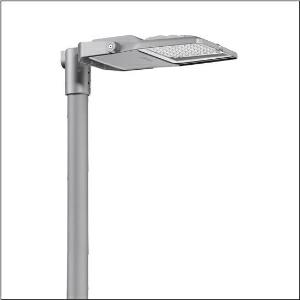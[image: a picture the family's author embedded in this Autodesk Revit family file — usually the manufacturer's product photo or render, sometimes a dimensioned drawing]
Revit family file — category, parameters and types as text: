
# Revit family: floodlight_fl_21_iq_mini___pl64_5xa7771b4e3a_3408
name_source: partatom
category: Lighting Fixtures
units: mm (PartAtom-declared; Revit-internal decimal feet)

## family parameters
Cut with Voids When Loaded = No
Host = Face
Light Source = No
Part Type = Normal
Room Calculation Point = No
Round Connector Dimension = Use Diameter
Shared = No

## types (1)
- --- (1 x LED, 6270 lm, 45.5 W, 4000K)
    Apparent Load = 46 VA
    CIE Flux Codes = 28 80 98 100 100
    Color Rendering = 70
    Color Temperature = 4000K
    Default Elevation = 1800 mm
    Description = Floodlight FL 21 iQ mini, floodlight, primary light control with lens, of PMMA, primary optical cover: protective disc, of toughened safety glass, transparent, light distribution: PL64, light emission: direct distribution, installation type: surface-mounted, LED, High Power LED, rated luminous flux: 6.270lm, luminous efficacy: 138lm/W, light colour: 740, colour temperature: 4000K, control: Auto-Match, Temp-Guard, Lumen-Switch, Night-Set, Smart-Wire, Light-Fading, Desk-Remote (wireless, voltage-free reading and setting of iQ features in the workshop via application-optimized NFC function/RFID function), optimised constant luminous flux control (CLO 2.0), with terminal, 6-pole, mains connection: 220..240V, AC, 50/60Hz, start of lifetime: 46W, end of service life: 48W, reduction: 22W, luminaire housing, of diecast aluminium, powder-coated, Siteco® metallic grey (DB 702S), corrosivity category C5 mid according to DIN EN ISO 12944, sealing non-destructively replaceable, please order mast flange separately, mast bracket, of steel, galvanised, powder-coated, Siteco® metallic grey (DB 702S), protection rating (complete): IP66, insulation class (complete): insulation class II (safety insulation), certification: CE, ENEC, VDE, protection symbol: D, impact resistance: IK08, permissible operating ambient temperature: -40..+40°C, permissible operating ambient temperature for outdoor applications: -40..+50°C, standard: DIN EN 12944, LABS conformity tested according to VDMA 24364:2018-05, packaging unit: 1 piece

Light Distribution: PL64
    Height = 70 mm
    Lamp = 1 x LED
    Lamp Light Flux = 6270 lm
    Lamp Power = 45.5 W
    Lamp count = 1
    Length = 485 mm
    Luminous efficacy = 138 lm/W
    Manufacturer = Siteco
    ModVariant = No
    Model = 5XA7771B4E3A
    Number of Poles = 1
    OnlyDefault = Yes
    Power Factor = 1
    Product Name = Floodlight FL 21 iQ mini | PL64
    Product group = floodlight | pylon annexe
    ProductGroupID = 6200
    Protection Class = Protection class II
    Protection Degree = IP 66
    RLX_Detail_Level = 1
    RLX_Emergency_Light_Flux = 0 lm
    RLX_Emergency_Type = 0
    RLX_Emergency_Type_DB = No
    RlxData = <blob elided: 101205 chars, md5=2ff61729>
    Socket = socket
    Standby Power = 0 W
    System Light Flux = 6270 lm
    System Power = 46 W
    Type Comments = factory setting: luminous flux: 100 % | dim-lin: 254 | 463 mA
    Type Image = l_1007125.jpg
    URL = http://relux.com
    VarID = @adj_137379
    Voltage = 0 V
    Weight = 0.00 kg
    Width = 337 mm

## geometry (parser evidence)
native form markers: Blend x4, Sweep x14
no freeform markers — native parametric forms only
